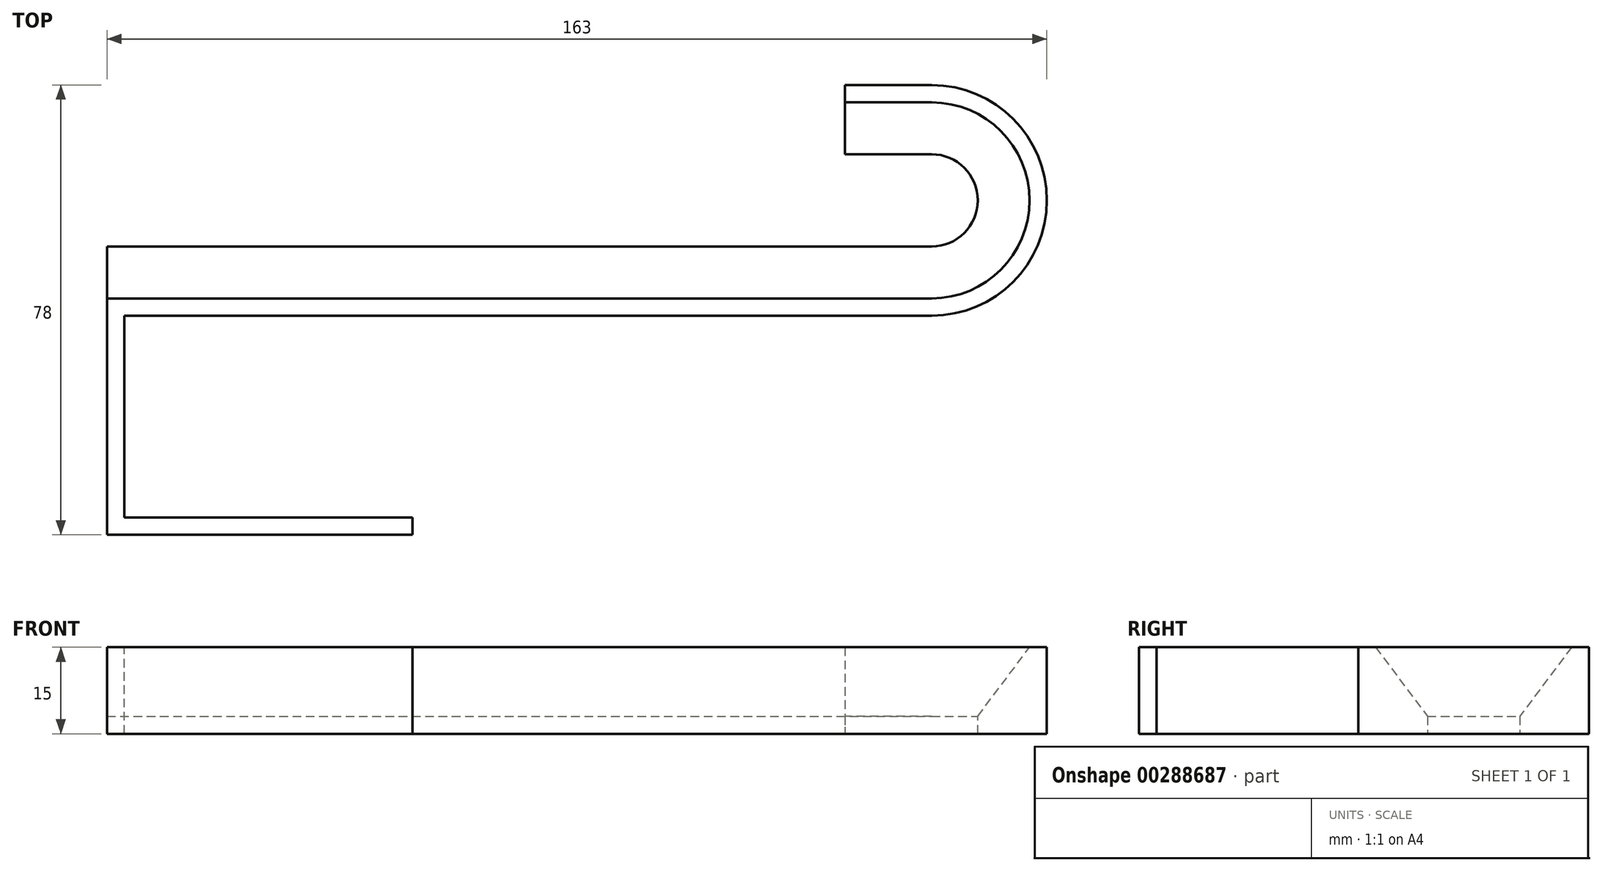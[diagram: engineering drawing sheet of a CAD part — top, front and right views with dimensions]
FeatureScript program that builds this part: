
annotation { "Feature Type Name" : "Feature", "Feature Type Description" : "" }
export const myFeature = defineFeature(function(context is Context, id is Id, definition is map)
    precondition{}
    {
        {
            var Q0;
            Q0=qCreatedBy(makeId("Top.planeOp"),FACE);
            var sketch = newSketch(context, id + "F0", { "sketchPlane" : qUnion([Q0])});
            skLineSegment(sketch, "E0", {"start": v(0, 0) * mm, "end": v(143, 0) * mm});
            skArc(sketch, "E1", {"start": v(143, 0) * mm, "mid": v(163, 20) * mm, "end": v(143, 40) * mm});
            skPoint(sketch, "E2", {"position": v(143, 0) * mm});
            skPoint(sketch, "E3", {"position": v(143, 40) * mm});
            skLineSegment(sketch, "E4", {"start": v(143, 40) * mm, "end": v(128, 40) * mm});
            skLineSegment(sketch, "E5", {"start": v(3, 0) * mm, "end": v(3, -35) * mm});
            skLineSegment(sketch, "E6", {"start": v(3, -35) * mm, "end": v(53, -35) * mm});
            skSolve(sketch);
        }
        {
            var Q0;
            Q0=qCreatedBy(makeId("Right.planeOp"),FACE);
            var sketch = newSketch(context, id + "F1", { "sketchPlane" : qUnion([Q0])});
            skLineSegment(sketch, "E7", {"start": v(0, 0) * mm, "end": v(12, 0) * mm});
            skLineSegment(sketch, "E8", {"start": v(0, 15) * mm, "end": v(0, 0) * mm});
            skLineSegment(sketch, "E9", {"start": v(0, 15) * mm, "end": v(3, 15) * mm});
            skLineSegment(sketch, "E10", {"start": v(3, 15) * mm, "end": v(3, 3) * mm});
            skLineSegment(sketch, "E11", {"start": v(3, 3) * mm, "end": v(12, 3) * mm});
            skLineSegment(sketch, "E12", {"start": v(12, 3) * mm, "end": v(12, 0) * mm});
            skLineSegment(sketch, "E13", {"start": v(3, 15) * mm, "end": v(12, 3) * mm});
            skSolve(sketch);
        }
        {
            var Q0;
            Q0=makeQuery(id+"F1.imprint","IMPRINT",FACE,{"disambiguationData":[TD([[makeQuery(id+"F1.imprint","IMPRINT",EDGE,{"derivedFrom":sQuery(id+"F1.wireOp",EDGE,"E7")}),1.0]])]});
            var Q1;
            Q1=makeQuery(id+"F1.imprint","IMPRINT",FACE,{"disambiguationData":[TD([[makeQuery(id+"F1.imprint","IMPRINT",EDGE,{"derivedFrom":sQuery(id+"F1.wireOp",EDGE,"E10")}),1.0]])]});
            var Q2;
            Q2=sQuery(id+"F0.wireOp",EDGE,"E0");
            var Q3;
            Q3=sQuery(id+"F0.wireOp",EDGE,"E1");
            var Q4;
            Q4=sQuery(id+"F0.wireOp",EDGE,"E4");
            sweep(context, id + "F2", {"profiles" : qUnion([Q0, Q1]), "path" : qUnion([Q2, Q3, Q4])});
        }
        {
            var Q0;
            Q0=makeQuery(id+"F2.opSweep","SWEPT_FACE",FACE,{"disambiguationData":[OSD([sQuery(id+"F0.wireOp",EDGE,"E0"),sQuery(id+"F1.wireOp",EDGE,"E8")])]});
            var sketch = newSketch(context, id + "F3", { "sketchPlane" : qUnion([Q0])});
            skLineSegment(sketch, "E14.bottom", {"start": v(0, 0) * mm, "end": v(3, 0) * mm});
            skLineSegment(sketch, "E14.top", {"start": v(0, 15) * mm, "end": v(3, 15) * mm});
            skLineSegment(sketch, "E14.left", {"start": v(0, 0) * mm, "end": v(0, 15) * mm});
            skLineSegment(sketch, "E14.right", {"start": v(3, 0) * mm, "end": v(3, 15) * mm});
            skSolve(sketch);
        }
        {
            var Q0;
            Q0=makeQuery(id+"F3.imprint","IMPRINT",FACE,{"disambiguationData":[TD([[makeQuery(id+"F3.imprint","IMPRINT",EDGE,{"derivedFrom":sQuery(id+"F3.wireOp",EDGE,"E14.bottom")}),1.0]])]});
            var Q1;
            Q1=sQuery(id+"F0.wireOp",EDGE,"E5");
            var Q2;
            Q2=sQuery(id+"F0.wireOp",EDGE,"E6");
            sweep(context, id + "F4", {"operationType" : NewBodyOperationType.ADD, "profiles" : qUnion([Q0]), "path" : qUnion([Q1, Q2])});
        }
    });
